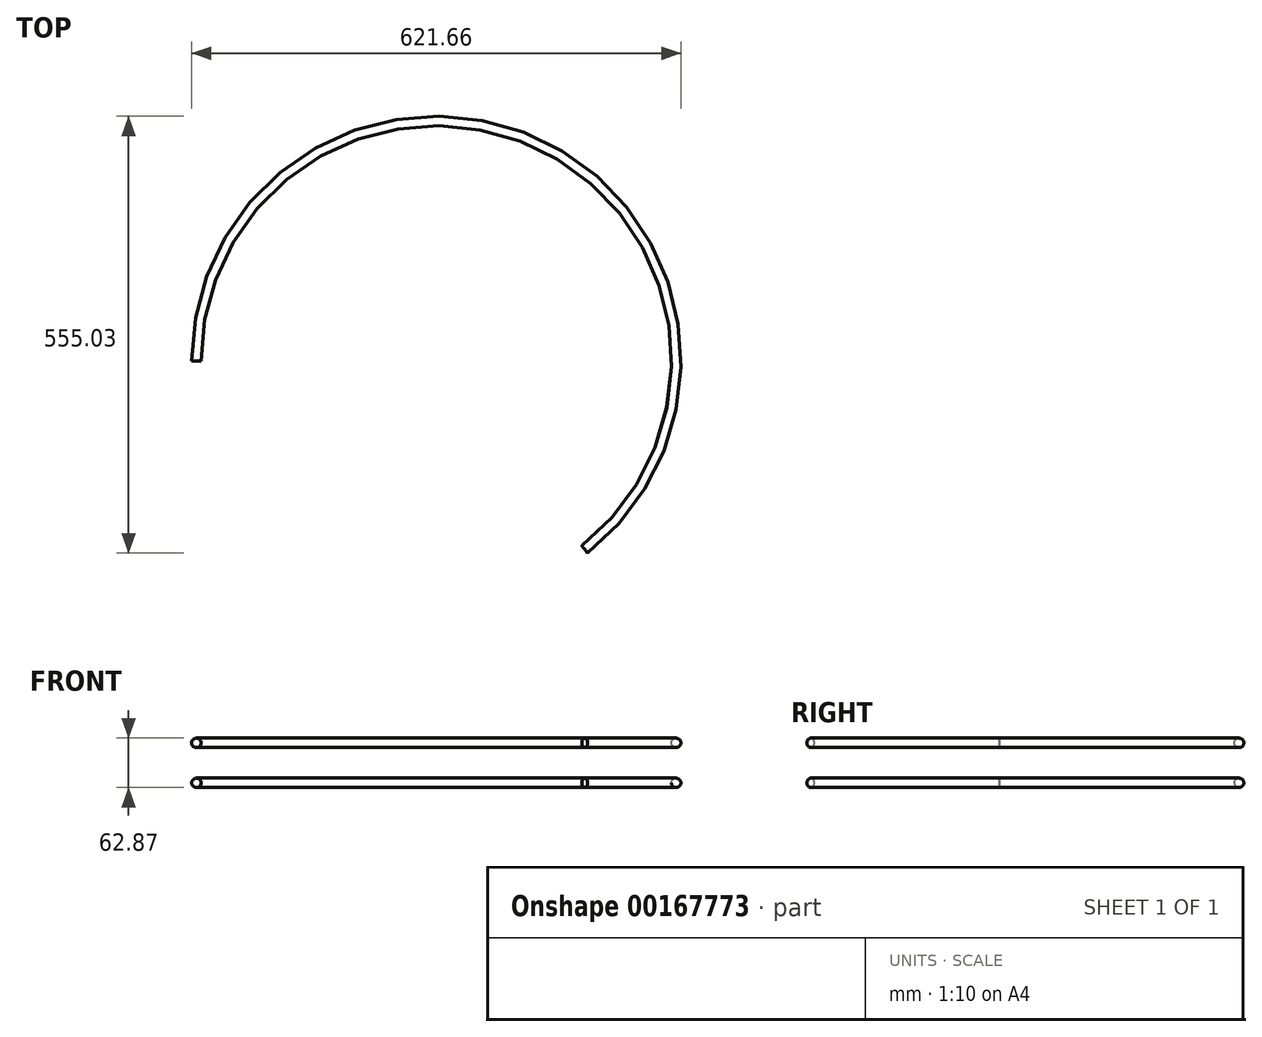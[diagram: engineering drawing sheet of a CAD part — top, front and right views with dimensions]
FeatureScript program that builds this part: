
annotation { "Feature Type Name" : "Feature", "Feature Type Description" : "" }
export const myFeature = defineFeature(function(context is Context, id is Id, definition is map)
    precondition{}
    {
        {
            var Q0;
            Q0=qCreatedBy(makeId("Top.planeOp"),FACE);
            var sketch = newSketch(context, id + "F0", { "sketchPlane" : qUnion([Q0])});
            skArc(sketch, "E0", {"start": v(188.58, -239.46) * mm, "mid": v(133.1, 274.2) * mm, "end": v(-304.8, 0.03) * mm});
            skSolve(sketch);
        }
        {
            var Q0;
            Q0=qCreatedBy(makeId("Top.planeOp"),FACE);
            cPlane(context, id + "F1", {"entities" : qUnion([Q0]), "cplaneType" : CPlaneType.OFFSET, "offset" : 50.8 * mm, "width" : 152.4 * mm, "height" : 152.4 * mm});
        }
        {
            var Q0;
            Q0=qCreatedBy(id+"F1.planeOp",FACE);
            var sketch = newSketch(context, id + "F2", { "sketchPlane" : qUnion([Q0])});
            skArc(sketch, "E1", {"start": v(188.58, -239.46) * mm, "mid": v(133.1, 274.2) * mm, "end": v(-304.8, 0.03) * mm});
            skSolve(sketch);
        }
        {
            var Q0;
            Q0=sQuery(id+"F2.wireOp",VERTEX,"E1.start");
            var Q1;
            Q1=sQuery(id+"F2.wireOp",EDGE,"E1");
            cPlane(context, id + "F3", {"entities" : qUnion([Q0, Q1]), "cplaneType" : CPlaneType.CURVE_POINT, "offset" : 25.4 * mm, "width" : 152.4 * mm, "height" : 152.4 * mm});
        }
        {
            var Q0;
            Q0=qCreatedBy(id+"F3.planeOp",FACE);
            var sketch = newSketch(context, id + "F4", { "sketchPlane" : qUnion([Q0])});
            skCircle(sketch, "E2", {"center": v(-304.8, 50.8) * mm, "radius": 6.03 * mm});
            skSolve(sketch);
        }
        {
            var Q0;
            Q0=qCreatedBy(id+"F3.planeOp",FACE);
            var sketch = newSketch(context, id + "F5", { "sketchPlane" : qUnion([Q0])});
            skCircle(sketch, "E3", {"center": v(-304.78, 0) * mm, "radius": 6.03 * mm});
            skSolve(sketch);
        }
        {
            var Q0;
            Q0=makeQuery(id+"F4.imprint","IMPRINT",FACE,{"disambiguationData":[TD([[makeQuery(id+"F4.imprint","IMPRINT",EDGE,{"derivedFrom":sQuery(id+"F4.wireOp",EDGE,"E2")}),1.0]])]});
            var Q1;
            Q1=sQuery(id+"F2.wireOp",EDGE,"E1");
            sweep(context, id + "F6", {"profiles" : qUnion([Q0]), "path" : qUnion([Q1])});
        }
        {
            var Q0;
            Q0=makeQuery(id+"F5.imprint","IMPRINT",FACE,{"disambiguationData":[TD([[makeQuery(id+"F5.imprint","IMPRINT",EDGE,{"derivedFrom":sQuery(id+"F5.wireOp",EDGE,"E3")}),1.0]])]});
            var Q1;
            Q1=sQuery(id+"F0.wireOp",EDGE,"E0");
            sweep(context, id + "F7", {"profiles" : qUnion([Q0]), "path" : qUnion([Q1])});
        }
    });
